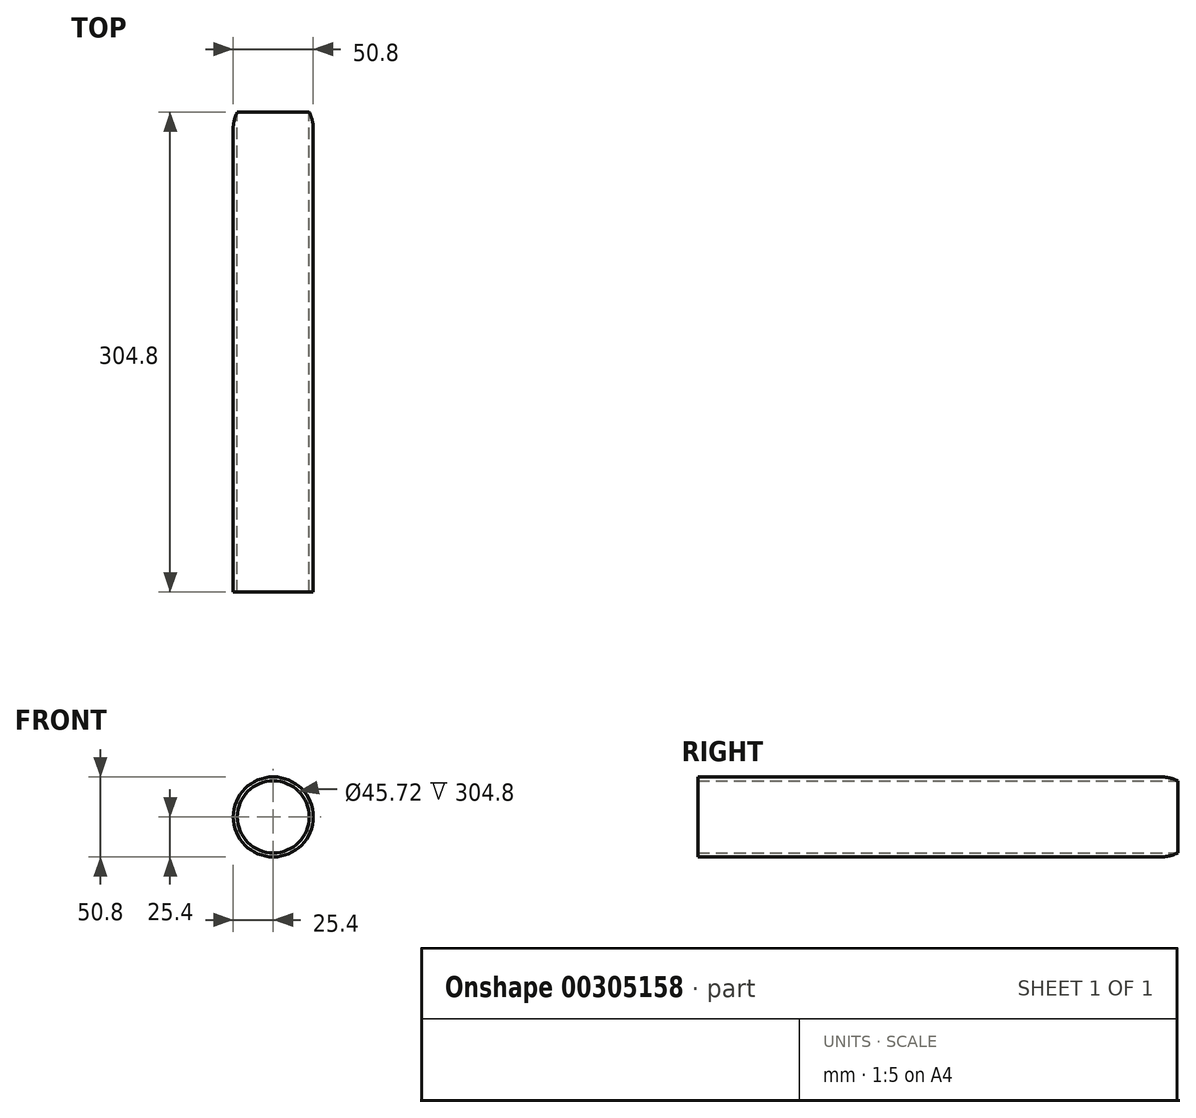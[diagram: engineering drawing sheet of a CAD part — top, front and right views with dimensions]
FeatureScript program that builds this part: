
annotation { "Feature Type Name" : "Feature", "Feature Type Description" : "" }
export const myFeature = defineFeature(function(context is Context, id is Id, definition is map)
    precondition{}
    {
        {
            var Q0;
            Q0=qCreatedBy(makeId("Right.planeOp"),FACE);
            var sketch = newSketch(context, id + "F0", { "sketchPlane" : qUnion([Q0])});
            skLineSegment(sketch, "E0.bottom", {"start": v(152.4, 12.7) * mm, "end": v(-152.4, 12.7) * mm});
            skLineSegment(sketch, "E0.top", {"start": v(152.4, -12.7) * mm, "end": v(-152.4, -12.7) * mm});
            skLineSegment(sketch, "E0.left", {"start": v(152.4, 12.7) * mm, "end": v(152.4, -12.7) * mm});
            skLineSegment(sketch, "E0.right", {"start": v(-152.4, 12.7) * mm, "end": v(-152.4, -12.7) * mm});
            skPoint(sketch, "E0.middle", {"position": v(0, 0) * mm});
            skLineSegment(sketch, "E1", {"start": v(-75.44, 0) * mm, "end": v(76.52, 0) * mm});
            skSolve(sketch);
        }
        {
            var Q0;
            Q0=makeQuery(id+"F0.imprint","IMPRINT",FACE,{"disambiguationData":[TD([[makeQuery(id+"F0.imprint","IMPRINT",EDGE,{"derivedFrom":sQuery(id+"F0.wireOp",EDGE,"E0.bottom")}),1.0]])]});
            var Q1;
            Q1=sQuery(id+"F0.wireOp",EDGE,"E0.top");
            revolve(context, id + "F1", {"entities" : qUnion([Q0]), "axis" : qUnion([Q1]), "revolveType" : RevolveType.SYMMETRIC, "angle" : 360 * degree});
        }
        {
            var Q0;
            Q0=makeQuery(id+"F1.opRevolve","SWEPT_FACE",FACE,{"disambiguationData":[OSD([sQuery(id+"F0.wireOp",EDGE,"E0.left")])]});
            var Q1;
            Q1=makeQuery(id+"F1.opRevolve","SWEPT_FACE",FACE,{"disambiguationData":[OSD([sQuery(id+"F0.wireOp",EDGE,"E0.right")])]});
            var Q2;
            Q2=makeQuery(id+"F1.opRevolve","SWEPT_BODY",BODY,{"disambiguationData":[OSD([sQuery(id+"F0.wireOp",EDGE,"E0.bottom"),sQuery(id+"F0.wireOp",EDGE,"E0.top"),sQuery(id+"F0.wireOp",EDGE,"E0.left"),sQuery(id+"F0.wireOp",EDGE,"E0.right")])]});
            shell(context, id + "F2", {"entities" : qUnion([Q0, Q1]), "parts" : qUnion([Q2]), "thickness" : 2.54 * mm});
        }
        {
            var Q0;
            Q0=makeQuery(id+"F1.opRevolve","SWEPT_EDGE",EDGE,{"disambiguationData":[OSD([sQuery(id+"F0.wireOp",EDGE,"E0.bottom"),sQuery(id+"F0.wireOp",EDGE,"E0.left")])]});
            fillet(context, id + "F3", {"entities" : qUnion([Q0]), "radius" : 22.86 * mm, "tangentPropagation" : true, "allowEdgeOverflow" : false});
        }
    });
